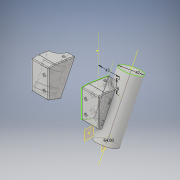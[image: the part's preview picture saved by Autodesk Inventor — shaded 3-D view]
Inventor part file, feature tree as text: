
AUTODESK INVENTOR PART (.ipt)
format: ipt  version: 2019.3 (Build 233278000, 278)  size: 306,176 bytes
history: native  units: mm
features: sketch x6, other x5, plane x4, hole x2, sweep x1, extrude x1, boolean_combine x1, revolve x1, fillet x1, mirror x1
ambient origin geometry x8: Origin, YZ Plane, XZ Plane, XY Plane, X Axis, Y Axis, Z Axis, Center Point
bodies: Body1 (feature_tree), Body2 (feature_tree), Body3 (feature_tree)
feature tree (23):
  other  "Stanchion"
  plane  "Work Plane2"
  sketch  "Sketch2"  dims[d4=0.0mm d5=0.0mm d8=10.0mm d9=0.0mm]
  plane  "Work Plane3"
  sweep  "Sweep1"
  plane  "Work Plane4"
  extrude  "Extrusion1"  Depth=28.0mm
  plane  "Work Plane5"
  hole  "Hole1"  [1 undecoded]
  boolean_combine  "Combine1"
  other  "Work Axis3"
  revolve  "Revolution1"  [1 undecoded]
  fillet  "Fillet3"  Radius=8.5mm
  hole  "Hole2"  [1 undecoded]
  mirror  "Mirror3"
  sketch  "Sketch3"  dims[d10=-69.25mm d11=28.0mm]
  sketch  "Sketch4"  dims[d12=5.5mm d13=6.0mm d14=9.3mm d15=54.75mm d16=90.0deg d17=8.0mm d18=20.594885mm d27=8.5mm]
  sketch  "Sketch6"  dims[d28=2.7mm d29=2.5mm d30=8.5mm]
  other  "DNM-USD8-FixRight"
  sketch  "Sketch9"  dims[d31=90.0deg d32=1.5mm]
  other  "Pattern of DNM-USD8-FixRight:2"
  other  "DNM-USD8-FixLeft"
  sketch  "Sketch10"  dims[d33=2.5mm d34=2.7mm d35=14.0mm d36=5.25mm d37=6.0mm d38=9.3mm d39=4.0mm d40=90.0deg d41=20.5mm d42=0.0mm d43=1.0mm d44=1.0mm d45=1.0mm d46=0.15mm d47=0.25mm d48=0.375mm d49=14.3117mm d50=0.75mm d51=20.594885mm d52=0.0625mm d53=0.75mm d54=0.375mm]
note: 3 required parameter values undecoded (feature->parameter linkage not recoverable at this tier; creation-order binding heuristic only, values carry confidence <= 0.55)